# Revit family: Sink-1.5 End Bowl-Clark Evolution Care RH
name_source: partatom
category: Plumbing Fixtures
revit_build: Autodesk Revit 2014 (Build: 20140709_2115(x64)
units: mm (PartAtom-declared; Revit-internal decimal feet)

## types (1)
- Evolution Care 1.5 End Bowl - 0TH
    1 Taphole = No
    3 Tapholes = No
    Assembly Code = D2010410
    CW Connection = No
    Capacity_ANZRS = 0.0 L
    Cost = 0 $
    Default Elevation = 0 mm  [stored 0 ft]
    Depth_ANZRS = 150 mm
    Description = The Clark Evolution sink collection includes a range of multi function accessories creating a total food preparation solution, its inspired Australian design features tight radius corners flowing to a flat sink base for a cutting edge geometric look.
    HW Connection = No
    Keynote = SK
    Length_ANZRS = 1035 mm
    Manufacturer = GWA Bathrooms & Kitchens
    Material_ANZRS = Metal-Stainless-Caroma
    Model = 4070
    ModifiedIssue_ANZRS = 20150617.01 $
    Spout Penetation = 100 mm  [stored 0.328084 ft]
    Tap Penetations = 100 mm  [stored 0.328084 ft]
    Type Comments = Clark Evolution Care 1.5 End Bowl - RH
    URL = http://specify.caroma.com.au
    Vent Connection = No
    WFU = 2
    Waste Connection = Yes
    Waste Radius = 30 mm  [stored 0.0984252 ft]
    Width_ANZRS = 460 mm

note: [stored X ft] marks values corroborated as IEEE doubles in the binary element streams (Revit-internal decimal feet)

## geometry (parser evidence)
native form markers: Blend x10, Sweep x2
no freeform markers — native parametric forms only
